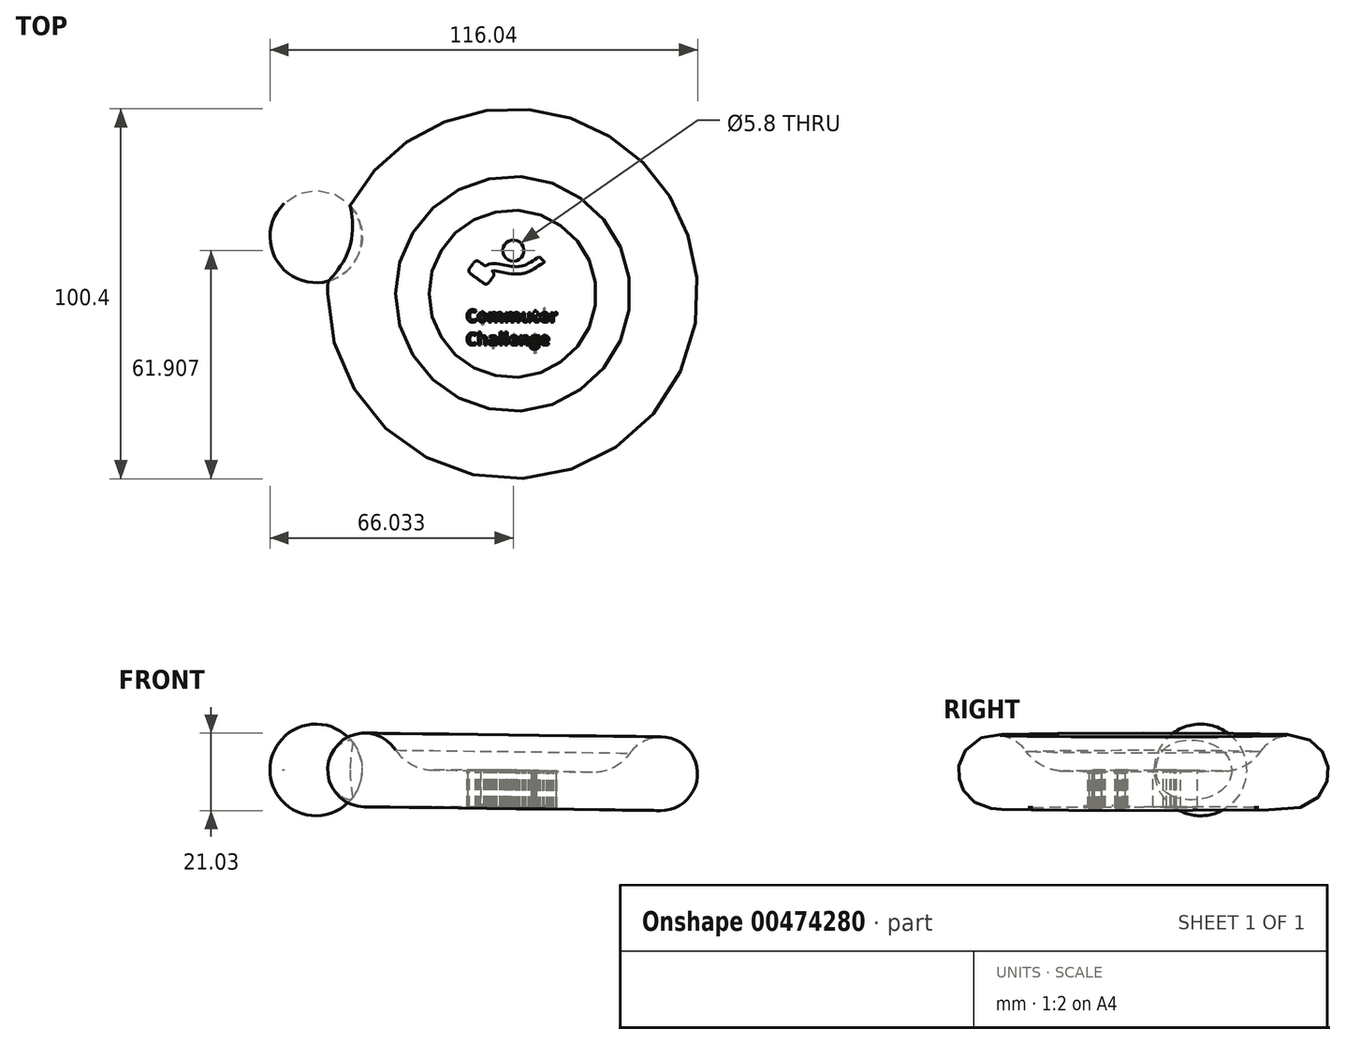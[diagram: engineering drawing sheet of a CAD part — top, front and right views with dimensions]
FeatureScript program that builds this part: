
annotation { "Feature Type Name" : "Feature", "Feature Type Description" : "" }
export const myFeature = defineFeature(function(context is Context, id is Id, definition is map)
    precondition{}
    {
        {
            var Q0;
            Q0=qCreatedBy(makeId("Top.planeOp"),FACE);
            var sketch = newSketch(context, id + "F0", { "sketchPlane" : qUnion([Q0])});
            skFitSpline(sketch, "E0", {"points": [v(-8.03, 7.42) * mm, v(-5.52, 8.24) * mm, v(1.63, 7.35) * mm, v(9.04, 11.01) * mm], "startDerivative": vector(15.74, 3.2) * mm, "endDerivative": vector(27.25, 14.63) * mm});
            skFitSpline(sketch, "E1", {"points": [v(-10.65, 1.76) * mm, v(-3.26, -0.1) * mm, v(1.18, 2.64) * mm, v(7.65, 4.6) * mm, v(11.91, -1.72) * mm], "startDerivative": vector(23.02, -28.98) * mm, "endDerivative": vector(3.27, -41.53) * mm});
            skLineSegment(sketch, "E2.bottom", {"start": v(-8.95, 8.72) * mm, "end": v(-5.33, 6.05) * mm});
            skLineSegment(sketch, "E2.top", {"start": v(-11.32, 5.5) * mm, "end": v(-7.7, 2.83) * mm});
            skLineSegment(sketch, "E2.left", {"start": v(-10.35, 8.51) * mm, "end": v(-11.53, 6.9) * mm});
            skLineSegment(sketch, "E2.right", {"start": v(-5.11, 4.65) * mm, "end": v(-6.3, 3.05) * mm});
            skPoint(sketch, "E3.visualSharp", {"position": v(-9.75, 9.32) * mm});
            skArc(sketch, "E3.filletArc", {"start": v(-8.95, 8.72) * mm, "mid": v(-9.7, 8.9) * mm, "end": v(-10.35, 8.51) * mm});
            skPoint(sketch, "E4.visualSharp", {"position": v(-12.13, 6.1) * mm});
            skArc(sketch, "E4.filletArc", {"start": v(-11.53, 6.9) * mm, "mid": v(-11.72, 6.16) * mm, "end": v(-11.32, 5.5) * mm});
            skPoint(sketch, "E5.visualSharp", {"position": v(-4.52, 5.46) * mm});
            skArc(sketch, "E5.filletArc", {"start": v(-5.11, 4.65) * mm, "mid": v(-4.93, 5.4) * mm, "end": v(-5.33, 6.05) * mm});
            skPoint(sketch, "E6.visualSharp", {"position": v(-7.7, 2.83) * mm});
            skArc(sketch, "E6.filletArc", {"start": v(-7.7, 2.83) * mm, "mid": v(-6.96, 2.65) * mm, "end": v(-6.3, 3.05) * mm});
            skLineSegment(sketch, "E7", {"start": v(7.4, 10.07) * mm, "end": v(8.81, 8.59) * mm});
            skFitSpline(sketch, "E8.0", {"points": [v(-12.22, 0.52) * mm, v(-11.9, 0.12) * mm, v(-11.22, -0.59) * mm, v(-10.08, -1.4) * mm, v(-8.87, -1.98) * mm, v(-7.23, -2.46) * mm, v(-5.23, -2.57) * mm, v(-3.42, -2.26) * mm, v(-2.14, -1.83) * mm, v(-1, -1.3) * mm, v(0.2, -0.54) * mm, v(1.4, 0.36) * mm, v(2.55, 1.17) * mm, v(3.91, 1.93) * mm, v(5.09, 2.4) * mm, v(5.96, 2.62) * mm, v(6.55, 2.7) * mm, v(7.06, 2.68) * mm, v(7.47, 2.6) * mm, v(7.86, 2.45) * mm, v(8.36, 2.13) * mm, v(8.98, 1.47) * mm, v(9.61, 0.13) * mm, v(9.86, -1.15) * mm, v(9.92, -1.88) * mm]});
            skLineSegment(sketch, "E9", {"start": v(-10.65, 1.76) * mm, "end": v(-12.06, 0.32) * mm});
            skLineSegment(sketch, "E10", {"start": v(9.9, -1.72) * mm, "end": v(11.91, -1.72) * mm});
            skCircle(sketch, "E11.0", {"center": v(0.33, 11.7) * mm, "radius": 2.9 * mm});
            skLineSegment(sketch, "E12", {"start": v(9.12, 16.34) * mm, "end": v(9.12, 16.34) * mm});
            skFitSpline(sketch, "E13.0", {"points": [v(-7.63, 5.46) * mm, v(-7.4, 5.51) * mm, v(-6.98, 5.62) * mm, v(-6.44, 5.82) * mm, v(-6.03, 6) * mm, v(-5.74, 6.14) * mm, v(-5.57, 6.21) * mm, v(-5.5, 6.23) * mm, v(-5.46, 6.24) * mm, v(-5.42, 6.24) * mm, v(-5.36, 6.25) * mm, v(-5.25, 6.25) * mm, v(-5.1, 6.24) * mm, v(-4.86, 6.22) * mm, v(-4.48, 6.18) * mm, v(-3.96, 6.09) * mm, v(-3.17, 5.94) * mm, v(-2.07, 5.72) * mm, v(-0.88, 5.52) * mm, v(0.1, 5.4) * mm, v(0.84, 5.34) * mm, v(1.47, 5.34) * mm, v(1.98, 5.37) * mm, v(2.72, 5.45) * mm, v(3.78, 5.7) * mm, v(5.02, 6.26) * mm, v(6.15, 6.91) * mm, v(7.26, 7.63) * mm, v(8.5, 8.4) * mm, v(9.46, 8.96) * mm, v(9.99, 9.25) * mm]});
            skText(sketch, "E14", { "text": "Commuter\nChallenge", "fontName": "OpenSans-Bold.ttf"});
            const initialGuessF0  = {"E14": [-0.0125, -0.00763, 1, 0, 0.00333]};
            skSetInitialGuess(sketch, initialGuessF0);
            skSolve(sketch);
        }
        {
            var Q0;
            Q0=qCreatedBy(makeId("Front.planeOp"),FACE);
            var sketch = newSketch(context, id + "F1", { "sketchPlane" : qUnion([Q0])});
            skArc(sketch, "E15", {"start": v(-31.64, 5.38) * mm, "mid": v(-48.85, 4.77) * mm, "end": v(-39.98, -10) * mm});
            skLineSegment(sketch, "E16.bottom", {"start": v(-39.98, -10) * mm, "end": v(0.02, -10) * mm});
            skLineSegment(sketch, "E16.right", {"start": v(0.02, -10) * mm, "end": v(0.14, 0) * mm});
            skLineSegment(sketch, "E17.trimOffspring", {"start": v(-22.52, 0) * mm, "end": v(0.14, 0) * mm});
            skArc(sketch, "E18", {"start": v(-31.64, 5.38) * mm, "mid": v(-27.67, 1.7) * mm, "end": v(-22.52, 0) * mm});
            skSolve(sketch);
        }
        {
            var Q0;
            Q0=makeQuery(id+"F1.imprint","IMPRINT",FACE,{"disambiguationData":[TD([[makeQuery(id+"F1.imprint","IMPRINT",EDGE,{"derivedFrom":sQuery(id+"F1.wireOp",EDGE,"E15")}),1.0]])]});
            var Q1;
            Q1=sQuery(id+"F1.wireOp",EDGE,"E16.right");
            revolve(context, id + "F2", {"entities" : qUnion([Q0]), "axis" : qUnion([Q1]), "revolveType" : RevolveType.FULL});
        }
        {
            var Q0;
            Q0=qCreatedBy(makeId("Top.planeOp"),FACE);
            var sketch = newSketch(context, id + "F3", { "sketchPlane" : qUnion([Q0])});
            skArc(sketch, "E19", {"start": v(-62.07, 24.32) * mm, "mid": v(-62.12, 6.6) * mm, "end": v(-44.4, 6.63) * mm});
            skLineSegment(sketch, "E20", {"start": v(-62.07, 24.32) * mm, "end": v(-44.4, 6.63) * mm});
            skSolve(sketch);
        }
        {
            var Q0;
            Q0=makeQuery(id+"F3.imprint","IMPRINT",FACE,{"disambiguationData":[TD([[makeQuery(id+"F3.imprint","IMPRINT",EDGE,{"derivedFrom":sQuery(id+"F3.wireOp",EDGE,"E19")}),1.0]])]});
            var Q1;
            Q1=sQuery(id+"F3.wireOp",EDGE,"E20");
            revolve(context, id + "F4", {"operationType" : NewBodyOperationType.REMOVE, "entities" : qUnion([Q0]), "axis" : qUnion([Q1]), "revolveType" : RevolveType.FULL, "oppositeDirection" : true});
        }
        {
            var Q0;
            Q0 = qSketchRegion(id + "F0", true);
            extrude(context, id + "F5", {"entities" : qUnion([Q0]), "operationType" : NewBodyOperationType.REMOVE, "endBound" : BoundingType.THROUGH_ALL, "oppositeDirection" : true, "depth" : 2 * mm});
        }
        {
            var Q0;
            Q0=makeQuery(id+"F5.boolean.opBoolean","INTERSECT",EDGE,{"derivedFrom":[makeQuery(id+"F2.opRevolve","SWEPT_FACE",FACE,{"disambiguationData":[OSD([sQuery(id+"F1.wireOp",EDGE,"E16.bottom")])]}),makeQuery(id+"F5.opExtrude","SWEPT_FACE",FACE,{"disambiguationData":[OSD([sQuery(id+"F0.wireOp",EDGE,"E14.sketch_text.stroke-126")])]})]});
            cPoint(context, id + "F6", {"entities" : qUnion([Q0]), "parameter" : 0.5});
        }
        {
            var Q0;
            Q0=makeQuery(id+"F5.boolean.opBoolean","INTERSECT",VERTEX,{"derivedFrom":[makeQuery(id+"F2.opRevolve","SWEPT_FACE",FACE,{"disambiguationData":[OSD([sQuery(id+"F1.wireOp",EDGE,"E16.bottom")])]}),makeQuery(id+"F5.opExtrude","SWEPT_FACE",FACE,{"disambiguationData":[OSD([sQuery(id+"F0.wireOp",EDGE,"E14.sketch_text.stroke-305")])]}),makeQuery(id+"F5.opExtrude","SWEPT_FACE",FACE,{"disambiguationData":[OSD([sQuery(id+"F0.wireOp",EDGE,"E14.sketch_text.stroke-306")])]})]});
            var Q1;
            Q1=makeQuery(id+"F5.boolean.opBoolean","INTERSECT",VERTEX,{"derivedFrom":[makeQuery(id+"F2.opRevolve","SWEPT_FACE",FACE,{"disambiguationData":[OSD([sQuery(id+"F1.wireOp",EDGE,"E16.bottom")])]}),makeQuery(id+"F5.opExtrude","SWEPT_FACE",FACE,{"disambiguationData":[OSD([sQuery(id+"F0.wireOp",EDGE,"E14.sketch_text.stroke-304")])]}),makeQuery(id+"F5.opExtrude","SWEPT_FACE",FACE,{"disambiguationData":[OSD([sQuery(id+"F0.wireOp",EDGE,"E14.sketch_text.stroke-305")])]})]});
            var Q2;
            Q2 = qCreatedBy(id + "F6" ,VERTEX);
            cPlane(context, id + "F7", {"entities" : qUnion([Q0, Q1, Q2]), "cplaneType" : CPlaneType.THREE_POINT, "offset" : 1 * mm, "oppositeDirection" : true, "width" : 150 * mm, "height" : 150 * mm});
        }
        {
            var Q0;
            Q0=qCreatedBy(id+"F7.planeOp",FACE);
            var sketch = newSketch(context, id + "F8", { "sketchPlane" : qUnion([Q0])});
            skLineSegment(sketch, "E21.bottom", {"start": v(9.25, -11.08) * mm, "end": v(8.86, -11.08) * mm});
            skLineSegment(sketch, "E21.top", {"start": v(9.25, -13.2) * mm, "end": v(8.86, -13.2) * mm});
            skLineSegment(sketch, "E21.left", {"start": v(9.25, -11.08) * mm, "end": v(9.25, -13.2) * mm});
            skLineSegment(sketch, "E21.right", {"start": v(8.86, -11.08) * mm, "end": v(8.86, -13.2) * mm});
            skLineSegment(sketch, "E22.bottom", {"start": v(6.63, -10.91) * mm, "end": v(6.16, -10.91) * mm});
            skLineSegment(sketch, "E22.top", {"start": v(6.63, -16.3) * mm, "end": v(6.16, -16.3) * mm});
            skLineSegment(sketch, "E22.left", {"start": v(6.63, -10.91) * mm, "end": v(6.63, -16.3) * mm});
            skLineSegment(sketch, "E22.right", {"start": v(6.16, -10.91) * mm, "end": v(6.16, -16.3) * mm});
            skLineSegment(sketch, "E23.bottom", {"start": v(0.86, -11) * mm, "end": v(0.63, -11) * mm});
            skLineSegment(sketch, "E23.top", {"start": v(0.86, -13.33) * mm, "end": v(0.63, -13.33) * mm});
            skLineSegment(sketch, "E23.left", {"start": v(0.86, -11) * mm, "end": v(0.86, -13.33) * mm});
            skLineSegment(sketch, "E23.right", {"start": v(0.63, -11) * mm, "end": v(0.63, -13.33) * mm});
            skLineSegment(sketch, "E24.bottom", {"start": v(-4.77, -12.19) * mm, "end": v(-5.12, -12.19) * mm});
            skLineSegment(sketch, "E24.top", {"start": v(-4.77, -15.03) * mm, "end": v(-5.12, -15.03) * mm});
            skLineSegment(sketch, "E24.left", {"start": v(-4.77, -12.19) * mm, "end": v(-4.77, -15.03) * mm});
            skLineSegment(sketch, "E24.right", {"start": v(-5.12, -12.19) * mm, "end": v(-5.12, -15.03) * mm});
            skLineSegment(sketch, "E25.bottom", {"start": v(-7.6, -4.67) * mm, "end": v(-8.11, -4.67) * mm});
            skLineSegment(sketch, "E25.top", {"start": v(-7.6, -8.5) * mm, "end": v(-8.11, -8.5) * mm});
            skLineSegment(sketch, "E25.left", {"start": v(-7.6, -4.67) * mm, "end": v(-7.6, -8.5) * mm});
            skLineSegment(sketch, "E25.right", {"start": v(-8.11, -4.67) * mm, "end": v(-8.11, -8.5) * mm});
            skLineSegment(sketch, "E26.bottom", {"start": v(9.21, -6.82) * mm, "end": v(8.87, -6.82) * mm});
            skLineSegment(sketch, "E26.top", {"start": v(9.21, -4.03) * mm, "end": v(8.87, -4.03) * mm});
            skLineSegment(sketch, "E26.left", {"start": v(9.21, -6.82) * mm, "end": v(9.21, -4.03) * mm});
            skLineSegment(sketch, "E26.right", {"start": v(8.87, -6.82) * mm, "end": v(8.87, -4.03) * mm});
            skSolve(sketch);
        }
        {
            var Q0;
            Q0 = qSketchRegion(id + "F8", true);
            extrude(context, id + "F9", {"entities" : qUnion([Q0]), "depth" : .5 * mm});
        }
    });
